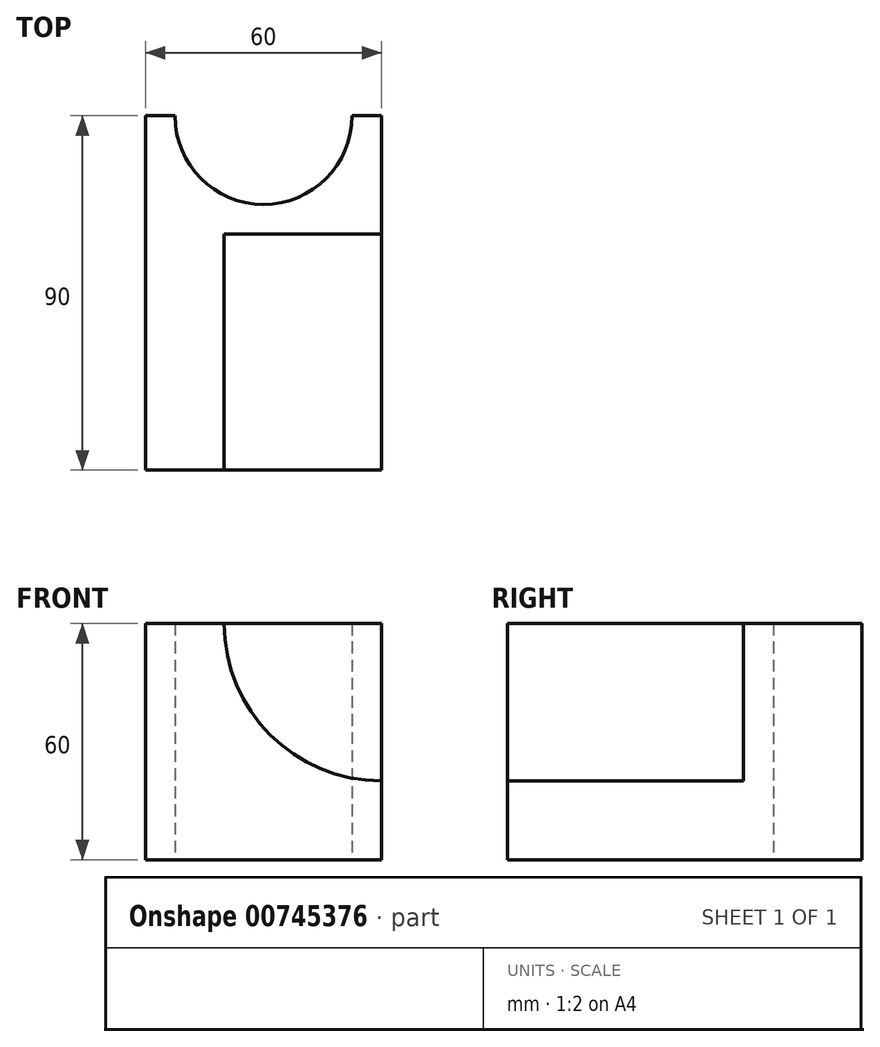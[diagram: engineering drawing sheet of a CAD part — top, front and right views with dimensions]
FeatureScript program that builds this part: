
annotation { "Feature Type Name" : "Feature", "Feature Type Description" : "" }
export const myFeature = defineFeature(function(context is Context, id is Id, definition is map)
    precondition{}
    {
        {
            var Q0;
            Q0=qCreatedBy(makeId("Top.planeOp"),FACE);
            var sketch = newSketch(context, id + "F0", { "sketchPlane" : qUnion([Q0])});
            skLineSegment(sketch, "E0", {"start": v(0, 90) * mm, "end": v(60, 90) * mm});
            skLineSegment(sketch, "E1", {"start": v(60, 90) * mm, "end": v(60, 0) * mm});
            skLineSegment(sketch, "E2", {"start": v(60, 0) * mm, "end": v(0, 0) * mm});
            skLineSegment(sketch, "E3", {"start": v(0, 0) * mm, "end": v(0, 90) * mm});
            skPoint(sketch, "E4", {"position": v(30, 90) * mm});
            skSolve(sketch);
        }
        {
            var Q0;
            Q0=makeQuery(id+"F0.imprint","IMPRINT",FACE,{"disambiguationData":[TD([[makeQuery(id+"F0.imprint","IMPRINT",EDGE,{"derivedFrom":sQuery(id+"F0.wireOp",EDGE,"E0")}),-1.0]])]});
            extrude(context, id + "F1", {"entities" : qUnion([Q0]), "depth" : 60 * mm, "offsetDistance" : 25 * mm});
        }
        {
            var Q0;
            Q0=qCreatedBy(makeId("Top.planeOp"),FACE);
            var sketch = newSketch(context, id + "F2", { "sketchPlane" : qUnion([Q0])});
            skArc(sketch, "E5", {"start": v(7.5, 90) * mm, "mid": v(30, 67.5) * mm, "end": v(52.5, 90) * mm});
            skLineSegment(sketch, "E6", {"start": v(52.5, 90) * mm, "end": v(30, 90) * mm});
            skLineSegment(sketch, "E7", {"start": v(30, 90) * mm, "end": v(7.5, 90) * mm});
            skSolve(sketch);
        }
        {
            var Q0;
            Q0 = qSketchRegion(id + "F2", true);
            extrude(context, id + "F3", {"entities" : qUnion([Q0]), "operationType" : NewBodyOperationType.REMOVE, "depth" : 60 * mm, "offsetDistance" : 25 * mm});
        }
        {
            var Q0;
            Q0=qCreatedBy(makeId("Front.planeOp"),FACE);
            var sketch = newSketch(context, id + "F4", { "sketchPlane" : qUnion([Q0])});
            skArc(sketch, "E8", {"start": v(20, 60) * mm, "mid": v(31.72, 31.72) * mm, "end": v(60, 20) * mm});
            skLineSegment(sketch, "E9", {"start": v(20, 60) * mm, "end": v(60, 60) * mm});
            skLineSegment(sketch, "E10", {"start": v(60, 20) * mm, "end": v(60, 60) * mm});
            skSolve(sketch);
        }
        {
            var Q0;
            Q0 = qSketchRegion(id + "F4", true);
            extrude(context, id + "F5", {"entities" : qUnion([Q0]), "operationType" : NewBodyOperationType.REMOVE, "oppositeDirection" : true, "depth" : 60 * mm, "offsetDistance" : 25 * mm});
        }
    });
